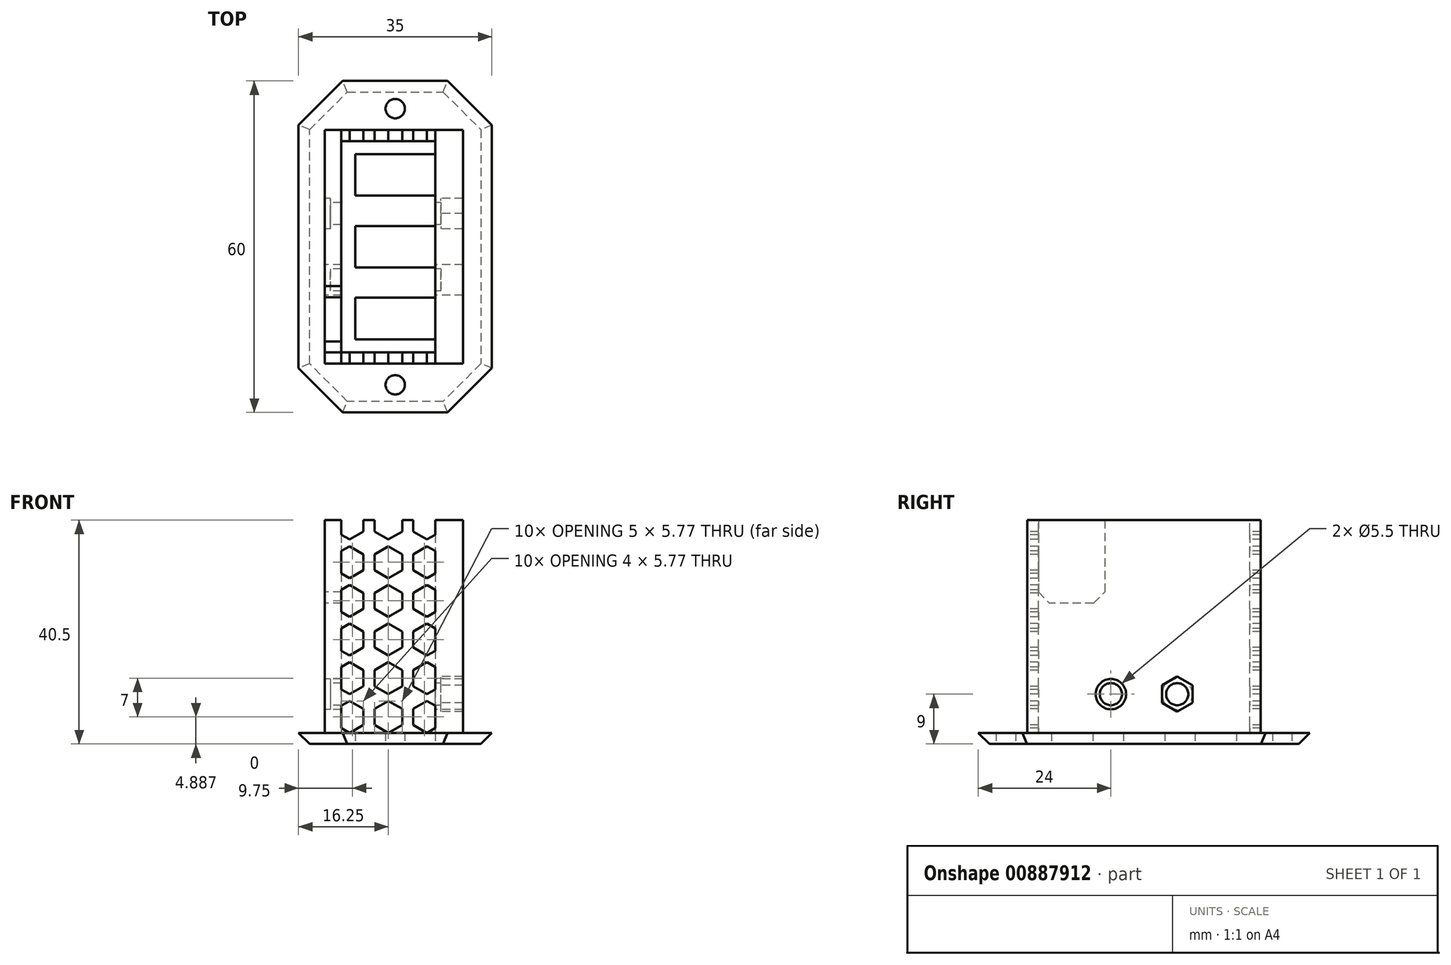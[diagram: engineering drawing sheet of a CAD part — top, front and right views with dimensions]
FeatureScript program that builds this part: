
annotation { "Feature Type Name" : "Feature", "Feature Type Description" : "" }
export const myFeature = defineFeature(function(context is Context, id is Id, definition is map)
    precondition{}
    {
        {
            var Q0;
            Q0=qCreatedBy(makeId("Top.planeOp"),FACE);
            var sketch = newSketch(context, id + "F0", { "sketchPlane" : qUnion([Q0])});
            skLineSegment(sketch, "E0.bottom", {"start": v(-17.5, 30) * mm, "end": v(17.5, 30) * mm});
            skLineSegment(sketch, "E0.top", {"start": v(-17.5, -30) * mm, "end": v(17.5, -30) * mm});
            skLineSegment(sketch, "E0.left", {"start": v(-17.5, 30) * mm, "end": v(-17.5, -30) * mm});
            skLineSegment(sketch, "E0.right", {"start": v(17.5, 30) * mm, "end": v(17.5, -30) * mm});
            skPoint(sketch, "E0.middle", {"position": v(0, 0) * mm});
            skLineSegment(sketch, "E1.bottom", {"start": v(-7.25, 16.75) * mm, "end": v(7.25, 16.75) * mm});
            skLineSegment(sketch, "E1.top", {"start": v(-7.25, 9.25) * mm, "end": v(7.25, 9.25) * mm});
            skLineSegment(sketch, "E1.left", {"start": v(-7.25, 16.75) * mm, "end": v(-7.25, 9.25) * mm});
            skLineSegment(sketch, "E1.right", {"start": v(7.25, 16.75) * mm, "end": v(7.25, 9.25) * mm});
            skPoint(sketch, "E1.middle", {"position": v(0, 13) * mm});
            skLineSegment(sketch, "E2.bottom", {"start": v(-7.25, 3.75) * mm, "end": v(7.25, 3.75) * mm});
            skLineSegment(sketch, "E2.top", {"start": v(-7.25, -3.75) * mm, "end": v(7.25, -3.75) * mm});
            skLineSegment(sketch, "E2.left", {"start": v(-7.25, 3.75) * mm, "end": v(-7.25, -3.75) * mm});
            skLineSegment(sketch, "E2.right", {"start": v(7.25, 3.75) * mm, "end": v(7.25, -3.75) * mm});
            skLineSegment(sketch, "E3.MirrorCS", {"start": v(-7.25, -16.75) * mm, "end": v(-7.25, -9.25) * mm});
            skLineSegment(sketch, "E4.MirrorCS", {"start": v(-7.25, -9.25) * mm, "end": v(7.25, -9.25) * mm});
            skLineSegment(sketch, "E5.MirrorCS", {"start": v(7.25, -16.75) * mm, "end": v(7.25, -9.25) * mm});
            skPoint(sketch, "E6.MirrorP", {"position": v(0, -13) * mm});
            skLineSegment(sketch, "E7.MirrorCS", {"start": v(-7.25, -16.75) * mm, "end": v(7.25, -16.75) * mm});
            skCircle(sketch, "E8", {"center": v(0, 25) * mm, "radius": 1.75 * mm});
            skCircle(sketch, "E9.MirrorC", {"center": v(0, -25) * mm, "radius": 1.75 * mm});
            skSolve(sketch);
        }
        {
            var Q0;
            Q0=makeQuery(id+"F0.imprint","IMPRINT",FACE,{"disambiguationData":[TD([[makeQuery(id+"F0.imprint","IMPRINT",EDGE,{"derivedFrom":sQuery(id+"F0.wireOp",EDGE,"E0.bottom")}),-1.0]])]});
            extrude(context, id + "F1", {"entities" : qUnion([Q0]), "depth" : 2 * mm, "offsetDistance" : 25 * mm});
        }
        {
            var Q0;
            Q0=makeQuery(id+"F1.opExtrude","CAP_FACE",FACE,{"disambiguationData":[OSD([sQuery(id+"F0.wireOp",EDGE,"E0.bottom"),sQuery(id+"F0.wireOp",EDGE,"E0.top"),sQuery(id+"F0.wireOp",EDGE,"E0.left"),sQuery(id+"F0.wireOp",EDGE,"E0.right"),sQuery(id+"F0.wireOp",EDGE,"E1.bottom"),sQuery(id+"F0.wireOp",EDGE,"E1.top"),sQuery(id+"F0.wireOp",EDGE,"E1.left"),sQuery(id+"F0.wireOp",EDGE,"E1.right"),sQuery(id+"F0.wireOp",EDGE,"E2.bottom"),sQuery(id+"F0.wireOp",EDGE,"E2.top"),sQuery(id+"F0.wireOp",EDGE,"E2.left"),sQuery(id+"F0.wireOp",EDGE,"E2.right"),sQuery(id+"F0.wireOp",EDGE,"E3.MirrorCS"),sQuery(id+"F0.wireOp",EDGE,"E4.MirrorCS"),sQuery(id+"F0.wireOp",EDGE,"E5.MirrorCS"),sQuery(id+"F0.wireOp",EDGE,"E7.MirrorCS"),sQuery(id+"F0.wireOp",EDGE,"E8"),sQuery(id+"F0.wireOp",EDGE,"E9.MirrorC")])],"isStart":false});
            var sketch = newSketch(context, id + "F2", { "sketchPlane" : qUnion([Q0])});
            skLineSegment(sketch, "E10.bottom", {"start": v(7.25, 19.12) * mm, "end": v(-9.75, 19.12) * mm});
            skLineSegment(sketch, "E10.top", {"start": v(7.25, -19.12) * mm, "end": v(-9.75, -19.12) * mm});
            skLineSegment(sketch, "E10.left", {"start": v(7.25, 19.12) * mm, "end": v(7.25, -19.12) * mm});
            skLineSegment(sketch, "E10.right", {"start": v(-9.75, 19.12) * mm, "end": v(-9.75, -19.13) * mm});
            skLineSegment(sketch, "E11", {"start": v(-1.25, 0) * mm, "end": v(-1.25, -19.12) * mm, "construction": true});
            skLineSegment(sketch, "E12.bottom", {"start": v(-12.75, 21.12) * mm, "end": v(12.25, 21.12) * mm});
            skLineSegment(sketch, "E12.top", {"start": v(-12.75, -21.12) * mm, "end": v(12.25, -21.12) * mm});
            skLineSegment(sketch, "E12.left", {"start": v(-12.75, 21.12) * mm, "end": v(-12.75, -21.12) * mm});
            skLineSegment(sketch, "E12.right", {"start": v(12.25, 21.12) * mm, "end": v(12.25, -21.12) * mm});
            skLineSegment(sketch, "E13", {"start": v(-1.25, 0) * mm, "end": v(-1.25, 19.12) * mm, "construction": true});
            skSolve(sketch);
        }
        {
            var Q0;
            {var subQ8=sQuery(id+"F2.wireOp",EDGE,"E10.bottom");Q0=makeQuery(id+"F2.imprint","IMPRINT",FACE,{"disambiguationData":[TD([[makeQuery(id+"F2.imprint","IMPRINT",EDGE,{"derivedFrom":subQ8}),-1.0]])]});}
            extrude(context, id + "F3", {"entities" : qUnion([Q0]), "operationType" : NewBodyOperationType.ADD, "depth" : 38.5 * mm, "offsetDistance" : 25 * mm});
        }
        {
            var Q0;
            Q0=makeQuery(id+"F3.opExtrude","SWEPT_FACE",FACE,{"disambiguationData":[OSD([sQuery(id+"F2.wireOp",EDGE,"E12.left")])]});
            var sketch = newSketch(context, id + "F4", { "sketchPlane" : qUnion([Q0])});
            skCircle(sketch, "E14", {"center": v(-6, 9) * mm, "radius": 2 * mm});
            skCircle(sketch, "E15.MirrorC", {"center": v(6, 9) * mm, "radius": 2 * mm});
            skLineSegment(sketch, "E16.bottom", {"start": v(7.12, 40.5) * mm, "end": v(19.12, 40.5) * mm});
            skLineSegment(sketch, "E16.top", {"start": v(7.12, 25.5) * mm, "end": v(19.12, 25.5) * mm});
            skLineSegment(sketch, "E16.left", {"start": v(7.12, 40.5) * mm, "end": v(7.12, 25.5) * mm});
            skLineSegment(sketch, "E16.right", {"start": v(19.12, 40.5) * mm, "end": v(19.12, 25.5) * mm});
            skCircle(sketch, "E17", {"center": v(-6, 9) * mm, "radius": 2.75 * mm});
            skCircle(sketch, "E18.MirrorC", {"center": v(6, 9) * mm, "radius": 2.75 * mm});
            skCircle(sketch, "E19.cCircle", {"center": v(-6, 9) * mm, "radius": 2.75 * mm, "construction": true});
            skLineSegment(sketch, "E19.0", {"start": v(-8.75, 7.41) * mm, "end": v(-8.75, 10.59) * mm});
            skLineSegment(sketch, "E19.1", {"start": v(-8.75, 10.59) * mm, "end": v(-6, 12.18) * mm});
            skLineSegment(sketch, "E19.2", {"start": v(-6, 12.18) * mm, "end": v(-3.25, 10.59) * mm});
            skLineSegment(sketch, "E19.3", {"start": v(-3.25, 10.59) * mm, "end": v(-3.25, 7.41) * mm});
            skLineSegment(sketch, "E19.4", {"start": v(-3.25, 7.41) * mm, "end": v(-6, 5.82) * mm});
            skLineSegment(sketch, "E19.5", {"start": v(-6, 5.82) * mm, "end": v(-8.75, 7.41) * mm});
            skPoint(sketch, "E19.0.midPoint", {"position": v(-8.75, 9) * mm});
            skLineSegment(sketch, "E20.MirrorCS", {"start": v(3.25, 10.59) * mm, "end": v(3.25, 7.41) * mm});
            skLineSegment(sketch, "E21.MirrorCS", {"start": v(6, 12.18) * mm, "end": v(3.25, 10.59) * mm});
            skLineSegment(sketch, "E22.MirrorCS", {"start": v(8.75, 10.59) * mm, "end": v(6, 12.18) * mm});
            skLineSegment(sketch, "E23.MirrorCS", {"start": v(8.75, 7.41) * mm, "end": v(8.75, 10.59) * mm});
            skLineSegment(sketch, "E24.MirrorCS", {"start": v(6, 5.82) * mm, "end": v(8.75, 7.41) * mm});
            skLineSegment(sketch, "E25.MirrorCS", {"start": v(3.25, 7.41) * mm, "end": v(6, 5.82) * mm});
            skSolve(sketch);
        }
        {
            var Q0;
            Q0=makeQuery(id+"F4.imprint","IMPRINT",FACE,{"disambiguationData":[TD([[makeQuery(id+"F4.imprint","IMPRINT",EDGE,{"derivedFrom":sQuery(id+"F4.wireOp",EDGE,"E14")}),1.0]])]});
            var Q1;
            Q1=makeQuery(id+"F4.imprint","IMPRINT",FACE,{"disambiguationData":[TD([[makeQuery(id+"F4.imprint","IMPRINT",EDGE,{"derivedFrom":sQuery(id+"F4.wireOp",EDGE,"E15.MirrorC")}),-1.0]])]});
            var Q2;
            Q2=makeQuery(id+"F3.opExtrude","SWEPT_FACE",FACE,{"disambiguationData":[OSD([sQuery(id+"F2.wireOp",EDGE,"E10.right")])]});
            extrude(context, id + "F5", {"entities" : qUnion([Q0, Q1]), "operationType" : NewBodyOperationType.REMOVE, "endBound" : BoundingType.THROUGH_ALL, "oppositeDirection" : true, "depth" : 25 * mm, "endBoundEntityFace" : qUnion([Q2]), "offsetDistance" : 25 * mm});
        }
        {
            var Q0;
            Q0=makeQuery(id+"F4.imprint","IMPRINT",FACE,{"disambiguationData":[TD([[makeQuery(id+"F4.imprint","IMPRINT",EDGE,{"derivedFrom":sQuery(id+"F4.wireOp",EDGE,"E16.bottom")}),-1.0]])]});
            var Q1;
            {var subQ0=sQuery(id+"F7.wireOp",EDGE,"a90cbd68-12bd-4cc1-b045-284ffa8241a5.0");Q1=makeQuery(id+"F8.boolean.opBoolean","MERGE",FACE,{"derivedFrom":[makeQuery(id+"F3.opExtrude","SWEPT_FACE",FACE,{"disambiguationData":[OSD([sQuery(id+"F2.wireOp",EDGE,"E10.right")])]})],"fromTools":[makeQuery(id+"F8.opExtrude","SWEPT_FACE",FACE,{"disambiguationData":[OSD([subQ0]),TDD([makeQuery(id+"F7.imprint","IMPRINT",EDGE,{"disambiguationData":[TD([[makeQuery(id+"F7.imprint","INTERSECT",VERTEX,{"derivedFrom":[sQuery(id+"F7.wireOp",EDGE,"1a68b521-4b53-484c-a319-d1eb5f4e1507.0.5.3"),subQ0]}),-1.0]])],"derivedFrom":subQ0})])]}),makeQuery(id+"F8.opExtrude","SWEPT_FACE",FACE,{"disambiguationData":[OSD([subQ0]),TDD([makeQuery(id+"F7.imprint","IMPRINT",EDGE,{"disambiguationData":[TD([[makeQuery(id+"F7.imprint","INTERSECT",VERTEX,{"derivedFrom":[sQuery(id+"F7.wireOp",EDGE,"1a68b521-4b53-484c-a319-d1eb5f4e1507.0.4.3"),subQ0]}),-1.0]])],"derivedFrom":subQ0})])]}),makeQuery(id+"F8.opExtrude","SWEPT_FACE",FACE,{"disambiguationData":[OSD([subQ0]),TDD([makeQuery(id+"F7.imprint","IMPRINT",EDGE,{"disambiguationData":[TD([[makeQuery(id+"F7.imprint","INTERSECT",VERTEX,{"derivedFrom":[sQuery(id+"F7.wireOp",EDGE,"1a68b521-4b53-484c-a319-d1eb5f4e1507.0.3.3"),subQ0]}),-1.0]])],"derivedFrom":subQ0})])]}),makeQuery(id+"F8.opExtrude","SWEPT_FACE",FACE,{"disambiguationData":[OSD([subQ0]),TDD([makeQuery(id+"F7.imprint","IMPRINT",EDGE,{"disambiguationData":[TD([[makeQuery(id+"F7.imprint","INTERSECT",VERTEX,{"derivedFrom":[sQuery(id+"F7.wireOp",EDGE,"1a68b521-4b53-484c-a319-d1eb5f4e1507.0.2.3"),subQ0]}),-1.0]])],"derivedFrom":subQ0})])]}),makeQuery(id+"F8.opExtrude","SWEPT_FACE",FACE,{"disambiguationData":[OSD([subQ0]),TDD([makeQuery(id+"F7.imprint","IMPRINT",EDGE,{"disambiguationData":[TD([[makeQuery(id+"F7.imprint","INTERSECT",VERTEX,{"derivedFrom":[sQuery(id+"F7.wireOp",EDGE,"1a68b521-4b53-484c-a319-d1eb5f4e1507.0.1.3"),subQ0]}),-1.0]])],"derivedFrom":subQ0})])]}),makeQuery(id+"F8.opExtrude","SWEPT_FACE",FACE,{"disambiguationData":[OSD([subQ0]),TDD([makeQuery(id+"F7.imprint","IMPRINT",EDGE,{"disambiguationData":[TD([[makeQuery(id+"F7.imprint","INTERSECT",VERTEX,{"derivedFrom":[sQuery(id+"F7.wireOp",EDGE,"cc298075-9ea3-4915-a283-5b18a67a5fa9.4"),subQ0]}),-1.0]])],"derivedFrom":subQ0})])]})]});}
            extrude(context, id + "F6", {"entities" : qUnion([Q0]), "operationType" : NewBodyOperationType.REMOVE, "endBound" : BoundingType.UP_TO_SURFACE, "oppositeDirection" : true, "depth" : 25 * mm, "endBoundEntityFace" : qUnion([Q1]), "offsetDistance" : 25 * mm});
        }
        {
            var Q0;
            Q0=makeQuery(id+"F3.opExtrude","SWEPT_FACE",FACE,{"disambiguationData":[OSD([sQuery(id+"F2.wireOp",EDGE,"E12.top")])]});
            var sketch = newSketch(context, id + "F7", { "sketchPlane" : qUnion([Q0])});
            skCircle(sketch, "E26.cCircle", {"center": v(-8.25, 4.89) * mm, "radius": 2.5 * mm, "construction": true});
            skLineSegment(sketch, "E26.0", {"start": v(-8.25, 7.77) * mm, "end": v(-5.75, 6.33) * mm});
            skLineSegment(sketch, "E26.1", {"start": v(-5.75, 6.33) * mm, "end": v(-5.75, 3.44) * mm});
            skLineSegment(sketch, "E26.2", {"start": v(-5.75, 3.44) * mm, "end": v(-8.25, 2) * mm});
            skLineSegment(sketch, "E26.3", {"start": v(-8.25, 2) * mm, "end": v(-10.75, 3.44) * mm});
            skLineSegment(sketch, "E26.4", {"start": v(-10.75, 3.44) * mm, "end": v(-10.75, 6.33) * mm});
            skLineSegment(sketch, "E26.5", {"start": v(-10.75, 6.33) * mm, "end": v(-8.25, 7.77) * mm});
            skPoint(sketch, "E26.0.midPoint", {"position": v(-7, 7.05) * mm});
            skLineSegment(sketch, "E27.0", {"start": v(-9.75, 40.5) * mm, "end": v(-9.75, 2) * mm});
            skLineSegment(sketch, "E28.0", {"start": v(7.25, 40.5) * mm, "end": v(7.25, 2) * mm});
            skLineSegment(sketch, "E29.0.1.0", {"start": v(-8.25, 14.77) * mm, "end": v(-5.75, 13.33) * mm});
            skLineSegment(sketch, "E29.0.1.1", {"start": v(-10.75, 10.44) * mm, "end": v(-10.75, 13.33) * mm});
            skLineSegment(sketch, "E29.0.1.2", {"start": v(-10.75, 13.33) * mm, "end": v(-8.25, 14.77) * mm});
            skPoint(sketch, "E29.0.1.3", {"position": v(-7, 14.05) * mm});
            skLineSegment(sketch, "E29.0.1.4", {"start": v(-5.75, 13.33) * mm, "end": v(-5.75, 10.44) * mm});
            skLineSegment(sketch, "E29.0.1.5", {"start": v(-5.75, 10.44) * mm, "end": v(-8.25, 9) * mm});
            skCircle(sketch, "E29.0.1.6", {"center": v(-8.25, 11.89) * mm, "radius": 2.5 * mm, "construction": true});
            skLineSegment(sketch, "E29.0.1.7", {"start": v(-8.25, 9) * mm, "end": v(-10.75, 10.44) * mm});
            skLineSegment(sketch, "E29.0.2.0", {"start": v(-8.25, 21.77) * mm, "end": v(-5.75, 20.33) * mm});
            skLineSegment(sketch, "E29.0.2.1", {"start": v(-10.75, 17.44) * mm, "end": v(-10.75, 20.33) * mm});
            skLineSegment(sketch, "E29.0.2.2", {"start": v(-10.75, 20.33) * mm, "end": v(-8.25, 21.77) * mm});
            skPoint(sketch, "E29.0.2.3", {"position": v(-7, 21.05) * mm});
            skLineSegment(sketch, "E29.0.2.4", {"start": v(-5.75, 20.33) * mm, "end": v(-5.75, 17.44) * mm});
            skLineSegment(sketch, "E29.0.2.5", {"start": v(-5.75, 17.44) * mm, "end": v(-8.25, 16) * mm});
            skCircle(sketch, "E29.0.2.6", {"center": v(-8.25, 18.89) * mm, "radius": 2.5 * mm, "construction": true});
            skLineSegment(sketch, "E29.0.2.7", {"start": v(-8.25, 16) * mm, "end": v(-10.75, 17.44) * mm});
            skLineSegment(sketch, "E29.0.3.0", {"start": v(-8.25, 28.77) * mm, "end": v(-5.75, 27.33) * mm});
            skLineSegment(sketch, "E29.0.3.1", {"start": v(-10.75, 24.44) * mm, "end": v(-10.75, 27.33) * mm});
            skLineSegment(sketch, "E29.0.3.2", {"start": v(-10.75, 27.33) * mm, "end": v(-8.25, 28.77) * mm});
            skPoint(sketch, "E29.0.3.3", {"position": v(-7, 28.05) * mm});
            skLineSegment(sketch, "E29.0.3.4", {"start": v(-5.75, 27.33) * mm, "end": v(-5.75, 24.44) * mm});
            skLineSegment(sketch, "E29.0.3.5", {"start": v(-5.75, 24.44) * mm, "end": v(-8.25, 23) * mm});
            skCircle(sketch, "E29.0.3.6", {"center": v(-8.25, 25.89) * mm, "radius": 2.5 * mm, "construction": true});
            skLineSegment(sketch, "E29.0.3.7", {"start": v(-8.25, 23) * mm, "end": v(-10.75, 24.44) * mm});
            skLineSegment(sketch, "E29.0.4.0", {"start": v(-8.25, 35.77) * mm, "end": v(-5.75, 34.33) * mm});
            skLineSegment(sketch, "E29.0.4.1", {"start": v(-10.75, 31.44) * mm, "end": v(-10.75, 34.33) * mm});
            skLineSegment(sketch, "E29.0.4.2", {"start": v(-10.75, 34.33) * mm, "end": v(-8.25, 35.77) * mm});
            skPoint(sketch, "E29.0.4.3", {"position": v(-7, 35.05) * mm});
            skLineSegment(sketch, "E29.0.4.4", {"start": v(-5.75, 34.33) * mm, "end": v(-5.75, 31.44) * mm});
            skLineSegment(sketch, "E29.0.4.5", {"start": v(-5.75, 31.44) * mm, "end": v(-8.25, 30) * mm});
            skCircle(sketch, "E29.0.4.6", {"center": v(-8.25, 32.89) * mm, "radius": 2.5 * mm, "construction": true});
            skLineSegment(sketch, "E29.0.4.7", {"start": v(-8.25, 30) * mm, "end": v(-10.75, 31.44) * mm});
            skLineSegment(sketch, "E29.0.5.0", {"start": v(-8.25, 42.77) * mm, "end": v(-5.75, 41.33) * mm});
            skLineSegment(sketch, "E29.0.5.1", {"start": v(-10.75, 38.44) * mm, "end": v(-10.75, 41.33) * mm});
            skLineSegment(sketch, "E29.0.5.2", {"start": v(-10.75, 41.33) * mm, "end": v(-8.25, 42.77) * mm});
            skPoint(sketch, "E29.0.5.3", {"position": v(-7, 42.05) * mm});
            skLineSegment(sketch, "E29.0.5.4", {"start": v(-5.75, 41.33) * mm, "end": v(-5.75, 38.44) * mm});
            skLineSegment(sketch, "E29.0.5.5", {"start": v(-5.75, 38.44) * mm, "end": v(-8.25, 37) * mm});
            skCircle(sketch, "E29.0.5.6", {"center": v(-8.25, 39.89) * mm, "radius": 2.5 * mm, "construction": true});
            skLineSegment(sketch, "E29.0.5.7", {"start": v(-8.25, 37) * mm, "end": v(-10.75, 38.44) * mm});
            skLineSegment(sketch, "E29.1.0.0", {"start": v(-1.25, 7.77) * mm, "end": v(1.25, 6.33) * mm});
            skLineSegment(sketch, "E29.1.0.1", {"start": v(-3.75, 3.44) * mm, "end": v(-3.75, 6.33) * mm});
            skLineSegment(sketch, "E29.1.0.2", {"start": v(-3.75, 6.33) * mm, "end": v(-1.25, 7.77) * mm});
            skPoint(sketch, "E29.1.0.3", {"position": v(0, 7.05) * mm});
            skLineSegment(sketch, "E29.1.0.4", {"start": v(1.25, 6.33) * mm, "end": v(1.25, 3.44) * mm});
            skLineSegment(sketch, "E29.1.0.5", {"start": v(1.25, 3.44) * mm, "end": v(-1.25, 2) * mm});
            skCircle(sketch, "E29.1.0.6", {"center": v(-1.25, 4.89) * mm, "radius": 2.5 * mm, "construction": true});
            skLineSegment(sketch, "E29.1.0.7", {"start": v(-1.25, 2) * mm, "end": v(-3.75, 3.44) * mm});
            skLineSegment(sketch, "E29.1.1.0", {"start": v(-1.25, 14.77) * mm, "end": v(1.25, 13.33) * mm});
            skLineSegment(sketch, "E29.1.1.1", {"start": v(-3.75, 10.44) * mm, "end": v(-3.75, 13.33) * mm});
            skLineSegment(sketch, "E29.1.1.2", {"start": v(-3.75, 13.33) * mm, "end": v(-1.25, 14.77) * mm});
            skPoint(sketch, "E29.1.1.3", {"position": v(0, 14.05) * mm});
            skLineSegment(sketch, "E29.1.1.4", {"start": v(1.25, 13.33) * mm, "end": v(1.25, 10.44) * mm});
            skLineSegment(sketch, "E29.1.1.5", {"start": v(1.25, 10.44) * mm, "end": v(-1.25, 9) * mm});
            skCircle(sketch, "E29.1.1.6", {"center": v(-1.25, 11.89) * mm, "radius": 2.5 * mm, "construction": true});
            skLineSegment(sketch, "E29.1.1.7", {"start": v(-1.25, 9) * mm, "end": v(-3.75, 10.44) * mm});
            skLineSegment(sketch, "E29.1.2.0", {"start": v(-1.25, 21.77) * mm, "end": v(1.25, 20.33) * mm});
            skLineSegment(sketch, "E29.1.2.1", {"start": v(-3.75, 17.44) * mm, "end": v(-3.75, 20.33) * mm});
            skLineSegment(sketch, "E29.1.2.2", {"start": v(-3.75, 20.33) * mm, "end": v(-1.25, 21.77) * mm});
            skPoint(sketch, "E29.1.2.3", {"position": v(0, 21.05) * mm});
            skLineSegment(sketch, "E29.1.2.4", {"start": v(1.25, 20.33) * mm, "end": v(1.25, 17.44) * mm});
            skLineSegment(sketch, "E29.1.2.5", {"start": v(1.25, 17.44) * mm, "end": v(-1.25, 16) * mm});
            skCircle(sketch, "E29.1.2.6", {"center": v(-1.25, 18.89) * mm, "radius": 2.5 * mm, "construction": true});
            skLineSegment(sketch, "E29.1.2.7", {"start": v(-1.25, 16) * mm, "end": v(-3.75, 17.44) * mm});
            skLineSegment(sketch, "E29.1.3.0", {"start": v(-1.25, 28.77) * mm, "end": v(1.25, 27.33) * mm});
            skLineSegment(sketch, "E29.1.3.1", {"start": v(-3.75, 24.44) * mm, "end": v(-3.75, 27.33) * mm});
            skLineSegment(sketch, "E29.1.3.2", {"start": v(-3.75, 27.33) * mm, "end": v(-1.25, 28.77) * mm});
            skPoint(sketch, "E29.1.3.3", {"position": v(0, 28.05) * mm});
            skLineSegment(sketch, "E29.1.3.4", {"start": v(1.25, 27.33) * mm, "end": v(1.25, 24.44) * mm});
            skLineSegment(sketch, "E29.1.3.5", {"start": v(1.25, 24.44) * mm, "end": v(-1.25, 23) * mm});
            skCircle(sketch, "E29.1.3.6", {"center": v(-1.25, 25.89) * mm, "radius": 2.5 * mm, "construction": true});
            skLineSegment(sketch, "E29.1.3.7", {"start": v(-1.25, 23) * mm, "end": v(-3.75, 24.44) * mm});
            skLineSegment(sketch, "E29.1.4.0", {"start": v(-1.25, 35.77) * mm, "end": v(1.25, 34.33) * mm});
            skLineSegment(sketch, "E29.1.4.1", {"start": v(-3.75, 31.44) * mm, "end": v(-3.75, 34.33) * mm});
            skLineSegment(sketch, "E29.1.4.2", {"start": v(-3.75, 34.33) * mm, "end": v(-1.25, 35.77) * mm});
            skPoint(sketch, "E29.1.4.3", {"position": v(0, 35.05) * mm});
            skLineSegment(sketch, "E29.1.4.4", {"start": v(1.25, 34.33) * mm, "end": v(1.25, 31.44) * mm});
            skLineSegment(sketch, "E29.1.4.5", {"start": v(1.25, 31.44) * mm, "end": v(-1.25, 30) * mm});
            skCircle(sketch, "E29.1.4.6", {"center": v(-1.25, 32.89) * mm, "radius": 2.5 * mm, "construction": true});
            skLineSegment(sketch, "E29.1.4.7", {"start": v(-1.25, 30) * mm, "end": v(-3.75, 31.44) * mm});
            skLineSegment(sketch, "E29.1.5.0", {"start": v(-1.25, 42.77) * mm, "end": v(1.25, 41.33) * mm});
            skLineSegment(sketch, "E29.1.5.1", {"start": v(-3.75, 38.44) * mm, "end": v(-3.75, 41.33) * mm});
            skLineSegment(sketch, "E29.1.5.2", {"start": v(-3.75, 41.33) * mm, "end": v(-1.25, 42.77) * mm});
            skPoint(sketch, "E29.1.5.3", {"position": v(0, 42.05) * mm});
            skLineSegment(sketch, "E29.1.5.4", {"start": v(1.25, 41.33) * mm, "end": v(1.25, 38.44) * mm});
            skLineSegment(sketch, "E29.1.5.5", {"start": v(1.25, 38.44) * mm, "end": v(-1.25, 37) * mm});
            skCircle(sketch, "E29.1.5.6", {"center": v(-1.25, 39.89) * mm, "radius": 2.5 * mm, "construction": true});
            skLineSegment(sketch, "E29.1.5.7", {"start": v(-1.25, 37) * mm, "end": v(-3.75, 38.44) * mm});
            skLineSegment(sketch, "E29.2.0.0", {"start": v(5.75, 7.77) * mm, "end": v(8.25, 6.33) * mm});
            skLineSegment(sketch, "E29.2.0.1", {"start": v(3.25, 3.44) * mm, "end": v(3.25, 6.33) * mm});
            skLineSegment(sketch, "E29.2.0.2", {"start": v(3.25, 6.33) * mm, "end": v(5.75, 7.77) * mm});
            skPoint(sketch, "E29.2.0.3", {"position": v(7, 7.05) * mm});
            skLineSegment(sketch, "E29.2.0.4", {"start": v(8.25, 6.33) * mm, "end": v(8.25, 3.44) * mm});
            skLineSegment(sketch, "E29.2.0.5", {"start": v(8.25, 3.44) * mm, "end": v(5.75, 2) * mm});
            skCircle(sketch, "E29.2.0.6", {"center": v(5.75, 4.89) * mm, "radius": 2.5 * mm, "construction": true});
            skLineSegment(sketch, "E29.2.0.7", {"start": v(5.75, 2) * mm, "end": v(3.25, 3.44) * mm});
            skLineSegment(sketch, "E29.2.1.0", {"start": v(5.75, 14.77) * mm, "end": v(8.25, 13.33) * mm});
            skLineSegment(sketch, "E29.2.1.1", {"start": v(3.25, 10.44) * mm, "end": v(3.25, 13.33) * mm});
            skLineSegment(sketch, "E29.2.1.2", {"start": v(3.25, 13.33) * mm, "end": v(5.75, 14.77) * mm});
            skPoint(sketch, "E29.2.1.3", {"position": v(7, 14.05) * mm});
            skLineSegment(sketch, "E29.2.1.4", {"start": v(8.25, 13.33) * mm, "end": v(8.25, 10.44) * mm});
            skLineSegment(sketch, "E29.2.1.5", {"start": v(8.25, 10.44) * mm, "end": v(5.75, 9) * mm});
            skCircle(sketch, "E29.2.1.6", {"center": v(5.75, 11.89) * mm, "radius": 2.5 * mm, "construction": true});
            skLineSegment(sketch, "E29.2.1.7", {"start": v(5.75, 9) * mm, "end": v(3.25, 10.44) * mm});
            skLineSegment(sketch, "E29.2.2.0", {"start": v(5.75, 21.77) * mm, "end": v(8.25, 20.33) * mm});
            skLineSegment(sketch, "E29.2.2.1", {"start": v(3.25, 17.44) * mm, "end": v(3.25, 20.33) * mm});
            skLineSegment(sketch, "E29.2.2.2", {"start": v(3.25, 20.33) * mm, "end": v(5.75, 21.77) * mm});
            skPoint(sketch, "E29.2.2.3", {"position": v(7, 21.05) * mm});
            skLineSegment(sketch, "E29.2.2.4", {"start": v(8.25, 20.33) * mm, "end": v(8.25, 17.44) * mm});
            skLineSegment(sketch, "E29.2.2.5", {"start": v(8.25, 17.44) * mm, "end": v(5.75, 16) * mm});
            skCircle(sketch, "E29.2.2.6", {"center": v(5.75, 18.89) * mm, "radius": 2.5 * mm, "construction": true});
            skLineSegment(sketch, "E29.2.2.7", {"start": v(5.75, 16) * mm, "end": v(3.25, 17.44) * mm});
            skLineSegment(sketch, "E29.2.3.0", {"start": v(5.75, 28.77) * mm, "end": v(8.25, 27.33) * mm});
            skLineSegment(sketch, "E29.2.3.1", {"start": v(3.25, 24.44) * mm, "end": v(3.25, 27.33) * mm});
            skLineSegment(sketch, "E29.2.3.2", {"start": v(3.25, 27.33) * mm, "end": v(5.75, 28.77) * mm});
            skPoint(sketch, "E29.2.3.3", {"position": v(7, 28.05) * mm});
            skLineSegment(sketch, "E29.2.3.4", {"start": v(8.25, 27.33) * mm, "end": v(8.25, 24.44) * mm});
            skLineSegment(sketch, "E29.2.3.5", {"start": v(8.25, 24.44) * mm, "end": v(5.75, 23) * mm});
            skCircle(sketch, "E29.2.3.6", {"center": v(5.75, 25.89) * mm, "radius": 2.5 * mm, "construction": true});
            skLineSegment(sketch, "E29.2.3.7", {"start": v(5.75, 23) * mm, "end": v(3.25, 24.44) * mm});
            skLineSegment(sketch, "E29.2.4.0", {"start": v(5.75, 35.77) * mm, "end": v(8.25, 34.33) * mm});
            skLineSegment(sketch, "E29.2.4.1", {"start": v(3.25, 31.44) * mm, "end": v(3.25, 34.33) * mm});
            skLineSegment(sketch, "E29.2.4.2", {"start": v(3.25, 34.33) * mm, "end": v(5.75, 35.77) * mm});
            skPoint(sketch, "E29.2.4.3", {"position": v(7, 35.05) * mm});
            skLineSegment(sketch, "E29.2.4.4", {"start": v(8.25, 34.33) * mm, "end": v(8.25, 31.44) * mm});
            skLineSegment(sketch, "E29.2.4.5", {"start": v(8.25, 31.44) * mm, "end": v(5.75, 30) * mm});
            skCircle(sketch, "E29.2.4.6", {"center": v(5.75, 32.89) * mm, "radius": 2.5 * mm, "construction": true});
            skLineSegment(sketch, "E29.2.4.7", {"start": v(5.75, 30) * mm, "end": v(3.25, 31.44) * mm});
            skLineSegment(sketch, "E29.2.5.0", {"start": v(5.75, 42.77) * mm, "end": v(8.25, 41.33) * mm});
            skLineSegment(sketch, "E29.2.5.1", {"start": v(3.25, 38.44) * mm, "end": v(3.25, 41.33) * mm});
            skLineSegment(sketch, "E29.2.5.2", {"start": v(3.25, 41.33) * mm, "end": v(5.75, 42.77) * mm});
            skPoint(sketch, "E29.2.5.3", {"position": v(7, 42.05) * mm});
            skLineSegment(sketch, "E29.2.5.4", {"start": v(8.25, 41.33) * mm, "end": v(8.25, 38.44) * mm});
            skLineSegment(sketch, "E29.2.5.5", {"start": v(8.25, 38.44) * mm, "end": v(5.75, 37) * mm});
            skCircle(sketch, "E29.2.5.6", {"center": v(5.75, 39.89) * mm, "radius": 2.5 * mm, "construction": true});
            skLineSegment(sketch, "E29.2.5.7", {"start": v(5.75, 37) * mm, "end": v(3.25, 38.44) * mm});
            skLineSegment(sketch, "E29.direction1", {"start": v(-8.25, 4.89) * mm, "end": v(-1.25, 4.89) * mm, "construction": true});
            skLineSegment(sketch, "E29.direction2", {"start": v(-8.25, 4.89) * mm, "end": v(-8.25, 11.89) * mm, "construction": true});
            skPoint(sketch, "E30", {"position": v(-9.75, 4.89) * mm});
            skPoint(sketch, "E31", {"position": v(7.25, 4.89) * mm});
            skSolve(sketch);
        }
        {
            var Q0;
            {var subQ1=sQuery(id+"F7.wireOp",EDGE,"E29.0.5.5");Q0=makeQuery(id+"F7.imprint","IMPRINT",FACE,{"disambiguationData":[TD([[makeQuery(id+"F7.imprint","IMPRINT",EDGE,{"derivedFrom":subQ1}),-1.0]])]});}
            var Q1;
            {var subQ1=sQuery(id+"F7.wireOp",EDGE,"E29.1.5.5");Q1=makeQuery(id+"F7.imprint","IMPRINT",FACE,{"disambiguationData":[TD([[makeQuery(id+"F7.imprint","IMPRINT",EDGE,{"derivedFrom":subQ1}),-1.0]])]});}
            var Q2;
            {var subQ0=sQuery(id+"F7.wireOp",EDGE,"E29.2.5.7");Q2=makeQuery(id+"F7.imprint","IMPRINT",FACE,{"disambiguationData":[TD([[makeQuery(id+"F7.imprint","IMPRINT",EDGE,{"derivedFrom":subQ0}),-1.0]])]});}
            var Q3;
            Q3=makeQuery(id+"F7.imprint","IMPRINT",FACE,{"disambiguationData":[TD([[makeQuery(id+"F7.imprint","IMPRINT",EDGE,{"derivedFrom":sQuery(id+"F7.wireOp",EDGE,"E29.2.4.1")}),-1.0]])]});
            var Q4;
            Q4=makeQuery(id+"F7.imprint","IMPRINT",FACE,{"disambiguationData":[TD([[makeQuery(id+"F7.imprint","IMPRINT",EDGE,{"derivedFrom":sQuery(id+"F7.wireOp",EDGE,"E29.1.4.0")}),-1.0]])]});
            var Q5;
            {var subQ1=sQuery(id+"F7.wireOp",EDGE,"E29.0.4.0");Q5=makeQuery(id+"F7.imprint","IMPRINT",FACE,{"disambiguationData":[TD([[makeQuery(id+"F7.imprint","IMPRINT",EDGE,{"derivedFrom":subQ1}),-1.0]])]});}
            var Q6;
            {var subQ1=sQuery(id+"F7.wireOp",EDGE,"E29.0.3.0");Q6=makeQuery(id+"F7.imprint","IMPRINT",FACE,{"disambiguationData":[TD([[makeQuery(id+"F7.imprint","IMPRINT",EDGE,{"derivedFrom":subQ1}),-1.0]])]});}
            var Q7;
            Q7=makeQuery(id+"F7.imprint","IMPRINT",FACE,{"disambiguationData":[TD([[makeQuery(id+"F7.imprint","IMPRINT",EDGE,{"derivedFrom":sQuery(id+"F7.wireOp",EDGE,"E29.1.3.0")}),-1.0]])]});
            var Q8;
            Q8=makeQuery(id+"F7.imprint","IMPRINT",FACE,{"disambiguationData":[TD([[makeQuery(id+"F7.imprint","IMPRINT",EDGE,{"derivedFrom":sQuery(id+"F7.wireOp",EDGE,"E29.2.3.1")}),-1.0]])]});
            var Q9;
            Q9=makeQuery(id+"F7.imprint","IMPRINT",FACE,{"disambiguationData":[TD([[makeQuery(id+"F7.imprint","IMPRINT",EDGE,{"derivedFrom":sQuery(id+"F7.wireOp",EDGE,"E29.2.2.1")}),-1.0]])]});
            var Q10;
            Q10=makeQuery(id+"F7.imprint","IMPRINT",FACE,{"disambiguationData":[TD([[makeQuery(id+"F7.imprint","IMPRINT",EDGE,{"derivedFrom":sQuery(id+"F7.wireOp",EDGE,"E29.1.2.0")}),-1.0]])]});
            var Q11;
            {var subQ1=sQuery(id+"F7.wireOp",EDGE,"E29.0.2.0");Q11=makeQuery(id+"F7.imprint","IMPRINT",FACE,{"disambiguationData":[TD([[makeQuery(id+"F7.imprint","IMPRINT",EDGE,{"derivedFrom":subQ1}),-1.0]])]});}
            var Q12;
            {var subQ1=sQuery(id+"F7.wireOp",EDGE,"E29.0.1.0");Q12=makeQuery(id+"F7.imprint","IMPRINT",FACE,{"disambiguationData":[TD([[makeQuery(id+"F7.imprint","IMPRINT",EDGE,{"derivedFrom":subQ1}),-1.0]])]});}
            var Q13;
            Q13=makeQuery(id+"F7.imprint","IMPRINT",FACE,{"disambiguationData":[TD([[makeQuery(id+"F7.imprint","IMPRINT",EDGE,{"derivedFrom":sQuery(id+"F7.wireOp",EDGE,"E29.1.1.0")}),-1.0]])]});
            var Q14;
            Q14=makeQuery(id+"F7.imprint","IMPRINT",FACE,{"disambiguationData":[TD([[makeQuery(id+"F7.imprint","IMPRINT",EDGE,{"derivedFrom":sQuery(id+"F7.wireOp",EDGE,"E29.2.1.1")}),-1.0]])]});
            var Q15;
            Q15=makeQuery(id+"F7.imprint","IMPRINT",FACE,{"disambiguationData":[TD([[makeQuery(id+"F7.imprint","IMPRINT",EDGE,{"derivedFrom":sQuery(id+"F7.wireOp",EDGE,"E29.2.0.1")}),-1.0]])]});
            var Q16;
            Q16=makeQuery(id+"F7.imprint","IMPRINT",FACE,{"disambiguationData":[TD([[makeQuery(id+"F7.imprint","IMPRINT",EDGE,{"derivedFrom":sQuery(id+"F7.wireOp",EDGE,"E29.1.0.0")}),-1.0]])]});
            var Q17;
            {var subQ4=sQuery(id+"F7.wireOp",EDGE,"E26.0");Q17=makeQuery(id+"F7.imprint","IMPRINT",FACE,{"disambiguationData":[TD([[makeQuery(id+"F7.imprint","IMPRINT",EDGE,{"derivedFrom":subQ4}),-1.0]])]});}
            var Q18;
            Q18=makeQuery(id+"F3.opExtrude","SWEPT_FACE",FACE,{"disambiguationData":[OSD([sQuery(id+"F2.wireOp",EDGE,"E12.bottom")])]});
            extrude(context, id + "F8", {"entities" : qUnion([Q0, Q1, Q2, Q3, Q4, Q5, Q6, Q7, Q8, Q9, Q10, Q11, Q12, Q13, Q14, Q15, Q16, Q17]), "operationType" : NewBodyOperationType.REMOVE, "endBound" : BoundingType.UP_TO_SURFACE, "oppositeDirection" : true, "depth" : 25 * mm, "endBoundEntityFace" : qUnion([Q18]), "offsetDistance" : 25 * mm});
        }
        {
            var Q0;
            Q0=makeQuery(id+"F1.opExtrude","SWEPT_EDGE",EDGE,{"disambiguationData":[OSD([sQuery(id+"F0.wireOp",EDGE,"E0.top"),sQuery(id+"F0.wireOp",EDGE,"E0.left")])]});
            var Q1;
            Q1=makeQuery(id+"F1.opExtrude","SWEPT_EDGE",EDGE,{"disambiguationData":[OSD([sQuery(id+"F0.wireOp",EDGE,"E0.top"),sQuery(id+"F0.wireOp",EDGE,"E0.right")])]});
            var Q2;
            Q2=makeQuery(id+"F1.opExtrude","SWEPT_EDGE",EDGE,{"disambiguationData":[OSD([sQuery(id+"F0.wireOp",EDGE,"E0.bottom"),sQuery(id+"F0.wireOp",EDGE,"E0.right")])]});
            var Q3;
            Q3=makeQuery(id+"F1.opExtrude","SWEPT_EDGE",EDGE,{"disambiguationData":[OSD([sQuery(id+"F0.wireOp",EDGE,"E0.bottom"),sQuery(id+"F0.wireOp",EDGE,"E0.left")])]});
            chamfer(context, id + "F9", {"entities" : qUnion([Q0, Q1, Q2, Q3]), "width" : 8 * mm, "tangentPropagation" : true});
        }
        {
            var Q0;
            {var subQ0=sQuery(id+"F0.wireOp",EDGE,"E0.left");var subQ1=sQuery(id+"F0.wireOp",EDGE,"E0.bottom");Q0=makeQuery(id+"F9.opChamfer","BLEND_EDGE",EDGE,{"blendedFrom":[makeQuery(id+"F1.opExtrude","SWEPT_EDGE",EDGE,{"disambiguationData":[OSD([subQ1,subQ0])]}),makeQuery(id+"F1.opExtrude","CAP_FACE",FACE,{"disambiguationData":[OSD([subQ1,sQuery(id+"F0.wireOp",EDGE,"E0.top"),subQ0,sQuery(id+"F0.wireOp",EDGE,"E0.right"),sQuery(id+"F0.wireOp",EDGE,"E1.bottom"),sQuery(id+"F0.wireOp",EDGE,"E1.top"),sQuery(id+"F0.wireOp",EDGE,"E1.left"),sQuery(id+"F0.wireOp",EDGE,"E1.right"),sQuery(id+"F0.wireOp",EDGE,"E2.bottom"),sQuery(id+"F0.wireOp",EDGE,"E2.top"),sQuery(id+"F0.wireOp",EDGE,"E2.left"),sQuery(id+"F0.wireOp",EDGE,"E2.right"),sQuery(id+"F0.wireOp",EDGE,"E3.MirrorCS"),sQuery(id+"F0.wireOp",EDGE,"E4.MirrorCS"),sQuery(id+"F0.wireOp",EDGE,"E5.MirrorCS"),sQuery(id+"F0.wireOp",EDGE,"E7.MirrorCS"),sQuery(id+"F0.wireOp",EDGE,"E8"),sQuery(id+"F0.wireOp",EDGE,"E9.MirrorC")])],"isStart":true})],"blendedInto":[makeQuery(id+"F1.opExtrude","CAP_FACE",FACE,{"disambiguationData":[OSD([subQ1,sQuery(id+"F0.wireOp",EDGE,"E0.top"),subQ0,sQuery(id+"F0.wireOp",EDGE,"E0.right"),sQuery(id+"F0.wireOp",EDGE,"E1.bottom"),sQuery(id+"F0.wireOp",EDGE,"E1.top"),sQuery(id+"F0.wireOp",EDGE,"E1.left"),sQuery(id+"F0.wireOp",EDGE,"E1.right"),sQuery(id+"F0.wireOp",EDGE,"E2.bottom"),sQuery(id+"F0.wireOp",EDGE,"E2.top"),sQuery(id+"F0.wireOp",EDGE,"E2.left"),sQuery(id+"F0.wireOp",EDGE,"E2.right"),sQuery(id+"F0.wireOp",EDGE,"E3.MirrorCS"),sQuery(id+"F0.wireOp",EDGE,"E4.MirrorCS"),sQuery(id+"F0.wireOp",EDGE,"E5.MirrorCS"),sQuery(id+"F0.wireOp",EDGE,"E7.MirrorCS"),sQuery(id+"F0.wireOp",EDGE,"E8"),sQuery(id+"F0.wireOp",EDGE,"E9.MirrorC")])],"isStart":true})]});}
            var Q1;
            Q1=makeQuery(id+"F1.opExtrude","CAP_EDGE",EDGE,{"disambiguationData":[OSD([sQuery(id+"F0.wireOp",EDGE,"E0.bottom")])],"isStart":true});
            var Q2;
            {var subQ0=sQuery(id+"F0.wireOp",EDGE,"E0.right");var subQ1=sQuery(id+"F0.wireOp",EDGE,"E0.bottom");Q2=makeQuery(id+"F9.opChamfer","BLEND_EDGE",EDGE,{"blendedFrom":[makeQuery(id+"F1.opExtrude","SWEPT_EDGE",EDGE,{"disambiguationData":[OSD([subQ1,subQ0])]}),makeQuery(id+"F1.opExtrude","CAP_FACE",FACE,{"disambiguationData":[OSD([subQ1,sQuery(id+"F0.wireOp",EDGE,"E0.top"),sQuery(id+"F0.wireOp",EDGE,"E0.left"),subQ0,sQuery(id+"F0.wireOp",EDGE,"E1.bottom"),sQuery(id+"F0.wireOp",EDGE,"E1.top"),sQuery(id+"F0.wireOp",EDGE,"E1.left"),sQuery(id+"F0.wireOp",EDGE,"E1.right"),sQuery(id+"F0.wireOp",EDGE,"E2.bottom"),sQuery(id+"F0.wireOp",EDGE,"E2.top"),sQuery(id+"F0.wireOp",EDGE,"E2.left"),sQuery(id+"F0.wireOp",EDGE,"E2.right"),sQuery(id+"F0.wireOp",EDGE,"E3.MirrorCS"),sQuery(id+"F0.wireOp",EDGE,"E4.MirrorCS"),sQuery(id+"F0.wireOp",EDGE,"E5.MirrorCS"),sQuery(id+"F0.wireOp",EDGE,"E7.MirrorCS"),sQuery(id+"F0.wireOp",EDGE,"E8"),sQuery(id+"F0.wireOp",EDGE,"E9.MirrorC")])],"isStart":true})],"blendedInto":[makeQuery(id+"F1.opExtrude","CAP_FACE",FACE,{"disambiguationData":[OSD([subQ1,sQuery(id+"F0.wireOp",EDGE,"E0.top"),sQuery(id+"F0.wireOp",EDGE,"E0.left"),subQ0,sQuery(id+"F0.wireOp",EDGE,"E1.bottom"),sQuery(id+"F0.wireOp",EDGE,"E1.top"),sQuery(id+"F0.wireOp",EDGE,"E1.left"),sQuery(id+"F0.wireOp",EDGE,"E1.right"),sQuery(id+"F0.wireOp",EDGE,"E2.bottom"),sQuery(id+"F0.wireOp",EDGE,"E2.top"),sQuery(id+"F0.wireOp",EDGE,"E2.left"),sQuery(id+"F0.wireOp",EDGE,"E2.right"),sQuery(id+"F0.wireOp",EDGE,"E3.MirrorCS"),sQuery(id+"F0.wireOp",EDGE,"E4.MirrorCS"),sQuery(id+"F0.wireOp",EDGE,"E5.MirrorCS"),sQuery(id+"F0.wireOp",EDGE,"E7.MirrorCS"),sQuery(id+"F0.wireOp",EDGE,"E8"),sQuery(id+"F0.wireOp",EDGE,"E9.MirrorC")])],"isStart":true})]});}
            var Q3;
            Q3=makeQuery(id+"F1.opExtrude","CAP_EDGE",EDGE,{"disambiguationData":[OSD([sQuery(id+"F0.wireOp",EDGE,"E0.right")])],"isStart":true});
            var Q4;
            {var subQ0=sQuery(id+"F0.wireOp",EDGE,"E0.right");var subQ1=sQuery(id+"F0.wireOp",EDGE,"E0.top");Q4=makeQuery(id+"F9.opChamfer","BLEND_EDGE",EDGE,{"blendedFrom":[makeQuery(id+"F1.opExtrude","SWEPT_EDGE",EDGE,{"disambiguationData":[OSD([subQ1,subQ0])]}),makeQuery(id+"F1.opExtrude","CAP_FACE",FACE,{"disambiguationData":[OSD([sQuery(id+"F0.wireOp",EDGE,"E0.bottom"),subQ1,sQuery(id+"F0.wireOp",EDGE,"E0.left"),subQ0,sQuery(id+"F0.wireOp",EDGE,"E1.bottom"),sQuery(id+"F0.wireOp",EDGE,"E1.top"),sQuery(id+"F0.wireOp",EDGE,"E1.left"),sQuery(id+"F0.wireOp",EDGE,"E1.right"),sQuery(id+"F0.wireOp",EDGE,"E2.bottom"),sQuery(id+"F0.wireOp",EDGE,"E2.top"),sQuery(id+"F0.wireOp",EDGE,"E2.left"),sQuery(id+"F0.wireOp",EDGE,"E2.right"),sQuery(id+"F0.wireOp",EDGE,"E3.MirrorCS"),sQuery(id+"F0.wireOp",EDGE,"E4.MirrorCS"),sQuery(id+"F0.wireOp",EDGE,"E5.MirrorCS"),sQuery(id+"F0.wireOp",EDGE,"E7.MirrorCS"),sQuery(id+"F0.wireOp",EDGE,"E8"),sQuery(id+"F0.wireOp",EDGE,"E9.MirrorC")])],"isStart":true})],"blendedInto":[makeQuery(id+"F1.opExtrude","CAP_FACE",FACE,{"disambiguationData":[OSD([sQuery(id+"F0.wireOp",EDGE,"E0.bottom"),subQ1,sQuery(id+"F0.wireOp",EDGE,"E0.left"),subQ0,sQuery(id+"F0.wireOp",EDGE,"E1.bottom"),sQuery(id+"F0.wireOp",EDGE,"E1.top"),sQuery(id+"F0.wireOp",EDGE,"E1.left"),sQuery(id+"F0.wireOp",EDGE,"E1.right"),sQuery(id+"F0.wireOp",EDGE,"E2.bottom"),sQuery(id+"F0.wireOp",EDGE,"E2.top"),sQuery(id+"F0.wireOp",EDGE,"E2.left"),sQuery(id+"F0.wireOp",EDGE,"E2.right"),sQuery(id+"F0.wireOp",EDGE,"E3.MirrorCS"),sQuery(id+"F0.wireOp",EDGE,"E4.MirrorCS"),sQuery(id+"F0.wireOp",EDGE,"E5.MirrorCS"),sQuery(id+"F0.wireOp",EDGE,"E7.MirrorCS"),sQuery(id+"F0.wireOp",EDGE,"E8"),sQuery(id+"F0.wireOp",EDGE,"E9.MirrorC")])],"isStart":true})]});}
            var Q5;
            Q5=makeQuery(id+"F1.opExtrude","CAP_EDGE",EDGE,{"disambiguationData":[OSD([sQuery(id+"F0.wireOp",EDGE,"E0.top")])],"isStart":true});
            var Q6;
            {var subQ0=sQuery(id+"F0.wireOp",EDGE,"E0.left");var subQ1=sQuery(id+"F0.wireOp",EDGE,"E0.top");Q6=makeQuery(id+"F9.opChamfer","BLEND_EDGE",EDGE,{"blendedFrom":[makeQuery(id+"F1.opExtrude","SWEPT_EDGE",EDGE,{"disambiguationData":[OSD([subQ1,subQ0])]}),makeQuery(id+"F1.opExtrude","CAP_FACE",FACE,{"disambiguationData":[OSD([sQuery(id+"F0.wireOp",EDGE,"E0.bottom"),subQ1,subQ0,sQuery(id+"F0.wireOp",EDGE,"E0.right"),sQuery(id+"F0.wireOp",EDGE,"E1.bottom"),sQuery(id+"F0.wireOp",EDGE,"E1.top"),sQuery(id+"F0.wireOp",EDGE,"E1.left"),sQuery(id+"F0.wireOp",EDGE,"E1.right"),sQuery(id+"F0.wireOp",EDGE,"E2.bottom"),sQuery(id+"F0.wireOp",EDGE,"E2.top"),sQuery(id+"F0.wireOp",EDGE,"E2.left"),sQuery(id+"F0.wireOp",EDGE,"E2.right"),sQuery(id+"F0.wireOp",EDGE,"E3.MirrorCS"),sQuery(id+"F0.wireOp",EDGE,"E4.MirrorCS"),sQuery(id+"F0.wireOp",EDGE,"E5.MirrorCS"),sQuery(id+"F0.wireOp",EDGE,"E7.MirrorCS"),sQuery(id+"F0.wireOp",EDGE,"E8"),sQuery(id+"F0.wireOp",EDGE,"E9.MirrorC")])],"isStart":true})],"blendedInto":[makeQuery(id+"F1.opExtrude","CAP_FACE",FACE,{"disambiguationData":[OSD([sQuery(id+"F0.wireOp",EDGE,"E0.bottom"),subQ1,subQ0,sQuery(id+"F0.wireOp",EDGE,"E0.right"),sQuery(id+"F0.wireOp",EDGE,"E1.bottom"),sQuery(id+"F0.wireOp",EDGE,"E1.top"),sQuery(id+"F0.wireOp",EDGE,"E1.left"),sQuery(id+"F0.wireOp",EDGE,"E1.right"),sQuery(id+"F0.wireOp",EDGE,"E2.bottom"),sQuery(id+"F0.wireOp",EDGE,"E2.top"),sQuery(id+"F0.wireOp",EDGE,"E2.left"),sQuery(id+"F0.wireOp",EDGE,"E2.right"),sQuery(id+"F0.wireOp",EDGE,"E3.MirrorCS"),sQuery(id+"F0.wireOp",EDGE,"E4.MirrorCS"),sQuery(id+"F0.wireOp",EDGE,"E5.MirrorCS"),sQuery(id+"F0.wireOp",EDGE,"E7.MirrorCS"),sQuery(id+"F0.wireOp",EDGE,"E8"),sQuery(id+"F0.wireOp",EDGE,"E9.MirrorC")])],"isStart":true})]});}
            var Q7;
            Q7=makeQuery(id+"F1.opExtrude","CAP_EDGE",EDGE,{"disambiguationData":[OSD([sQuery(id+"F0.wireOp",EDGE,"E0.left")])],"isStart":true});
            chamfer(context, id + "F10", {"entities" : qUnion([Q0, Q1, Q2, Q3, Q4, Q5, Q6, Q7]), "width" : 2 * mm, "tangentPropagation" : true});
        }
        {
            var Q0;
            {var subQ2=sQuery(id+"F0.wireOp",EDGE,"E1.top");var subQ5=sQuery(id+"F2.wireOp",EDGE,"E10.left");Q0=makeQuery(id+"F3.boolean.opBoolean","SPLIT",EDGE,{"disambiguationData":[TD([makeQuery(id+"F1.opExtrude","SWEPT_FACE",FACE,{"disambiguationData":[OSD([subQ2])]})])],"derivedFrom":makeQuery(id+"F3.opExtrude","CAP_EDGE",EDGE,{"disambiguationData":[OSD([subQ5])],"isStart":true})});}
            var Q1;
            {var subQ3=sQuery(id+"F0.wireOp",EDGE,"E2.top");var subQ5=sQuery(id+"F2.wireOp",EDGE,"E10.left");Q1=makeQuery(id+"F3.boolean.opBoolean","SPLIT",EDGE,{"disambiguationData":[TD([makeQuery(id+"F1.opExtrude","SWEPT_FACE",FACE,{"disambiguationData":[OSD([subQ3])]})])],"derivedFrom":makeQuery(id+"F3.opExtrude","CAP_EDGE",EDGE,{"disambiguationData":[OSD([subQ5])],"isStart":true})});}
            var Q2;
            Q2=makeQuery(id+"F6.boolean.opBoolean","COPY",EDGE,{"derivedFrom":makeQuery(id+"F6.opExtrude","SWEPT_EDGE",EDGE,{"disambiguationData":[OSD([sQuery(id+"F4.wireOp",EDGE,"E16.top"),sQuery(id+"F4.wireOp",EDGE,"E16.left")])]})});
            var Q3;
            Q3=makeQuery(id+"F6.boolean.opBoolean","COPY",EDGE,{"derivedFrom":makeQuery(id+"F6.opExtrude","SWEPT_EDGE",EDGE,{"disambiguationData":[OSD([sQuery(id+"F4.wireOp",EDGE,"E16.top"),sQuery(id+"F4.wireOp",EDGE,"E16.right")])]})});
            var Q4;
            Q4=makeQuery(id+"F6.boolean.opBoolean","COPY",EDGE,{"derivedFrom":makeQuery(id+"F6.opExtrude","SWEPT_EDGE",EDGE,{"disambiguationData":[OSD([sQuery(id+"F2.wireOp",EDGE,"6b8dd937-4b73-436f-8f68-6c4afc0a345a.3"),sQuery(id+"F4.wireOp",EDGE,"E16.bottom"),sQuery(id+"F4.wireOp",EDGE,"E16.left")])]})});
            chamfer(context, id + "F11", {"entities" : qUnion([Q0, Q1, Q2, Q3, Q4]), "width" : 2 * mm, "tangentPropagation" : true});
        }
        {
            var Q0;
            Q0=makeQuery(id+"F4.imprint","IMPRINT",FACE,{"disambiguationData":[TD([[makeQuery(id+"F4.imprint","IMPRINT",EDGE,{"derivedFrom":sQuery(id+"F4.wireOp",EDGE,"E14")}),-1.0]])]});
            var Q1;
            Q1=makeQuery(id+"F4.imprint","IMPRINT",FACE,{"disambiguationData":[TD([[makeQuery(id+"F4.imprint","IMPRINT",EDGE,{"derivedFrom":sQuery(id+"F4.wireOp",EDGE,"E15.MirrorC")}),1.0]])]});
            extrude(context, id + "F12", {"entities" : qUnion([Q0, Q1]), "operationType" : NewBodyOperationType.REMOVE, "oppositeDirection" : true, "depth" : 1 * mm, "offsetDistance" : 25 * mm});
        }
        {
            var Q0;
            Q0=makeQuery(id+"F4.imprint","IMPRINT",FACE,{"disambiguationData":[TD([[makeQuery(id+"F4.imprint","IMPRINT",EDGE,{"derivedFrom":sQuery(id+"F4.wireOp",EDGE,"E15.MirrorC")}),1.0]])]});
            var Q1;
            Q1=makeQuery(id+"F4.imprint","IMPRINT",FACE,{"disambiguationData":[TD([[makeQuery(id+"F4.imprint","IMPRINT",EDGE,{"derivedFrom":sQuery(id+"F4.wireOp",EDGE,"E14")}),1.0]])]});
            var Q2;
            Q2=makeQuery(id+"F4.imprint","IMPRINT",FACE,{"disambiguationData":[TD([[makeQuery(id+"F4.imprint","IMPRINT",EDGE,{"derivedFrom":sQuery(id+"F4.wireOp",EDGE,"E14")}),-1.0]])]});
            var Q3;
            Q3=makeQuery(id+"F4.imprint","IMPRINT",FACE,{"disambiguationData":[TD([[makeQuery(id+"F4.imprint","IMPRINT",EDGE,{"derivedFrom":sQuery(id+"F4.wireOp",EDGE,"E15.MirrorC")}),-1.0]])]});
            var Q4;
            {var subQ0=sQuery(id+"F4.wireOp",EDGE,"E19.2");var subQ1=sQuery(id+"F4.wireOp",EDGE,"E17");var subQ2=makeQuery(id+"F4.imprint","INTERSECT",VERTEX,{"derivedFrom":[subQ1,subQ0]});Q4=makeQuery(id+"F4.imprint","IMPRINT",FACE,{"disambiguationData":[TD([[makeQuery(id+"F4.imprint","IMPRINT",EDGE,{"disambiguationData":[TD([[subQ2,1.0]])],"derivedFrom":subQ1}),-1.0]])]});}
            var Q5;
            {var subQ0=sQuery(id+"F4.wireOp",EDGE,"E24.MirrorCS");var subQ1=sQuery(id+"F4.wireOp",EDGE,"E18.MirrorC");var subQ2=makeQuery(id+"F4.imprint","INTERSECT",VERTEX,{"derivedFrom":[subQ1,subQ0]});Q5=makeQuery(id+"F4.imprint","IMPRINT",FACE,{"disambiguationData":[TD([[makeQuery(id+"F4.imprint","IMPRINT",EDGE,{"disambiguationData":[TD([[subQ2,-1.0]])],"derivedFrom":subQ1}),1.0]])]});}
            var Q6;
            {var subQ0=sQuery(id+"F4.wireOp",EDGE,"E23.MirrorCS");var subQ1=sQuery(id+"F4.wireOp",EDGE,"E18.MirrorC");var subQ2=makeQuery(id+"F4.imprint","INTERSECT",VERTEX,{"derivedFrom":[subQ1,subQ0]});Q6=makeQuery(id+"F4.imprint","IMPRINT",FACE,{"disambiguationData":[TD([[makeQuery(id+"F4.imprint","IMPRINT",EDGE,{"disambiguationData":[TD([[subQ2,-1.0]])],"derivedFrom":subQ1}),1.0]])]});}
            var Q7;
            {var subQ0=sQuery(id+"F4.wireOp",EDGE,"E19.3");var subQ1=sQuery(id+"F4.wireOp",EDGE,"E17");var subQ2=makeQuery(id+"F4.imprint","INTERSECT",VERTEX,{"derivedFrom":[subQ1,subQ0]});Q7=makeQuery(id+"F4.imprint","IMPRINT",FACE,{"disambiguationData":[TD([[makeQuery(id+"F4.imprint","IMPRINT",EDGE,{"disambiguationData":[TD([[subQ2,1.0]])],"derivedFrom":subQ1}),-1.0]])]});}
            var Q8;
            {var subQ0=sQuery(id+"F4.wireOp",EDGE,"E22.MirrorCS");var subQ1=sQuery(id+"F4.wireOp",EDGE,"E18.MirrorC");var subQ2=makeQuery(id+"F4.imprint","INTERSECT",VERTEX,{"derivedFrom":[subQ1,subQ0]});Q8=makeQuery(id+"F4.imprint","IMPRINT",FACE,{"disambiguationData":[TD([[makeQuery(id+"F4.imprint","IMPRINT",EDGE,{"disambiguationData":[TD([[subQ2,-1.0]])],"derivedFrom":subQ1}),1.0]])]});}
            var Q9;
            {var subQ0=sQuery(id+"F4.wireOp",EDGE,"E20.MirrorCS");var subQ1=sQuery(id+"F4.wireOp",EDGE,"E18.MirrorC");var subQ2=makeQuery(id+"F4.imprint","INTERSECT",VERTEX,{"derivedFrom":[subQ1,subQ0]});Q9=makeQuery(id+"F4.imprint","IMPRINT",FACE,{"disambiguationData":[TD([[makeQuery(id+"F4.imprint","IMPRINT",EDGE,{"disambiguationData":[TD([[subQ2,1.0]])],"derivedFrom":subQ1}),1.0]])]});}
            var Q10;
            {var subQ0=sQuery(id+"F4.wireOp",EDGE,"E19.2");var subQ1=sQuery(id+"F4.wireOp",EDGE,"E17");var subQ2=makeQuery(id+"F4.imprint","INTERSECT",VERTEX,{"derivedFrom":[subQ1,subQ0]});Q10=makeQuery(id+"F4.imprint","IMPRINT",FACE,{"disambiguationData":[TD([[makeQuery(id+"F4.imprint","IMPRINT",EDGE,{"disambiguationData":[TD([[subQ2,-1.0]])],"derivedFrom":subQ1}),-1.0]])]});}
            var Q11;
            {var subQ0=sQuery(id+"F4.wireOp",EDGE,"E19.5");var subQ1=sQuery(id+"F4.wireOp",EDGE,"E17");var subQ2=makeQuery(id+"F4.imprint","INTERSECT",VERTEX,{"derivedFrom":[subQ1,subQ0]});Q11=makeQuery(id+"F4.imprint","IMPRINT",FACE,{"disambiguationData":[TD([[makeQuery(id+"F4.imprint","IMPRINT",EDGE,{"disambiguationData":[TD([[subQ2,-1.0]])],"derivedFrom":subQ1}),-1.0]])]});}
            var Q12;
            {var subQ0=sQuery(id+"F4.wireOp",EDGE,"E19.1");var subQ1=sQuery(id+"F4.wireOp",EDGE,"E17");var subQ2=makeQuery(id+"F4.imprint","INTERSECT",VERTEX,{"derivedFrom":[subQ1,subQ0]});Q12=makeQuery(id+"F4.imprint","IMPRINT",FACE,{"disambiguationData":[TD([[makeQuery(id+"F4.imprint","IMPRINT",EDGE,{"disambiguationData":[TD([[subQ2,-1.0]])],"derivedFrom":subQ1}),-1.0]])]});}
            var Q13;
            {var subQ0=sQuery(id+"F4.wireOp",EDGE,"E21.MirrorCS");var subQ1=sQuery(id+"F4.wireOp",EDGE,"E18.MirrorC");var subQ2=makeQuery(id+"F4.imprint","INTERSECT",VERTEX,{"derivedFrom":[subQ1,subQ0]});Q13=makeQuery(id+"F4.imprint","IMPRINT",FACE,{"disambiguationData":[TD([[makeQuery(id+"F4.imprint","IMPRINT",EDGE,{"disambiguationData":[TD([[subQ2,-1.0]])],"derivedFrom":subQ1}),1.0]])]});}
            var Q14;
            {var subQ0=sQuery(id+"F4.wireOp",EDGE,"E21.MirrorCS");var subQ1=sQuery(id+"F4.wireOp",EDGE,"E18.MirrorC");var subQ2=makeQuery(id+"F4.imprint","INTERSECT",VERTEX,{"derivedFrom":[subQ1,subQ0]});Q14=makeQuery(id+"F4.imprint","IMPRINT",FACE,{"disambiguationData":[TD([[makeQuery(id+"F4.imprint","IMPRINT",EDGE,{"disambiguationData":[TD([[subQ2,1.0]])],"derivedFrom":subQ1}),1.0]])]});}
            var Q15;
            {var subQ0=sQuery(id+"F4.wireOp",EDGE,"E19.0");var subQ1=sQuery(id+"F4.wireOp",EDGE,"E17");var subQ2=makeQuery(id+"F4.imprint","INTERSECT",VERTEX,{"derivedFrom":[subQ1,subQ0]});Q15=makeQuery(id+"F4.imprint","IMPRINT",FACE,{"disambiguationData":[TD([[makeQuery(id+"F4.imprint","IMPRINT",EDGE,{"disambiguationData":[TD([[subQ2,-1.0]])],"derivedFrom":subQ1}),-1.0]])]});}
            var Q16;
            Q16=makeQuery(id+"F3.opExtrude","SWEPT_FACE",FACE,{"disambiguationData":[OSD([sQuery(id+"F2.wireOp",EDGE,"E12.right")])]});
            var Q17;
            Q17=makeQuery(id+"F3.opExtrude","SWEPT_FACE",FACE,{"disambiguationData":[OSD([sQuery(id+"F2.wireOp",EDGE,"E12.right")])]});
            extrude(context, id + "F13", {"entities" : qUnion([Q0, Q1, Q2, Q3, Q4, Q5, Q6, Q7, Q8, Q9, Q10, Q11, Q12, Q13, Q14, Q15]), "operationType" : NewBodyOperationType.REMOVE, "endBound" : BoundingType.UP_TO_SURFACE, "oppositeDirection" : true, "depth" : 25 * mm, "endBoundEntityFace" : qUnion([Q16]), "offsetDistance" : 25 * mm, "hasSecondDirection" : true, "secondDirectionBound" : SecondDirectionBoundingType.UP_TO_SURFACE, "secondDirectionOppositeDirection" : true, "secondDirectionDepth" : 25 * mm, "secondDirectionBoundEntityFace" : qUnion([Q17]), "hasSecondDirectionOffset" : true, "secondDirectionOffsetDistance" : 4 * mm});
        }
    });
